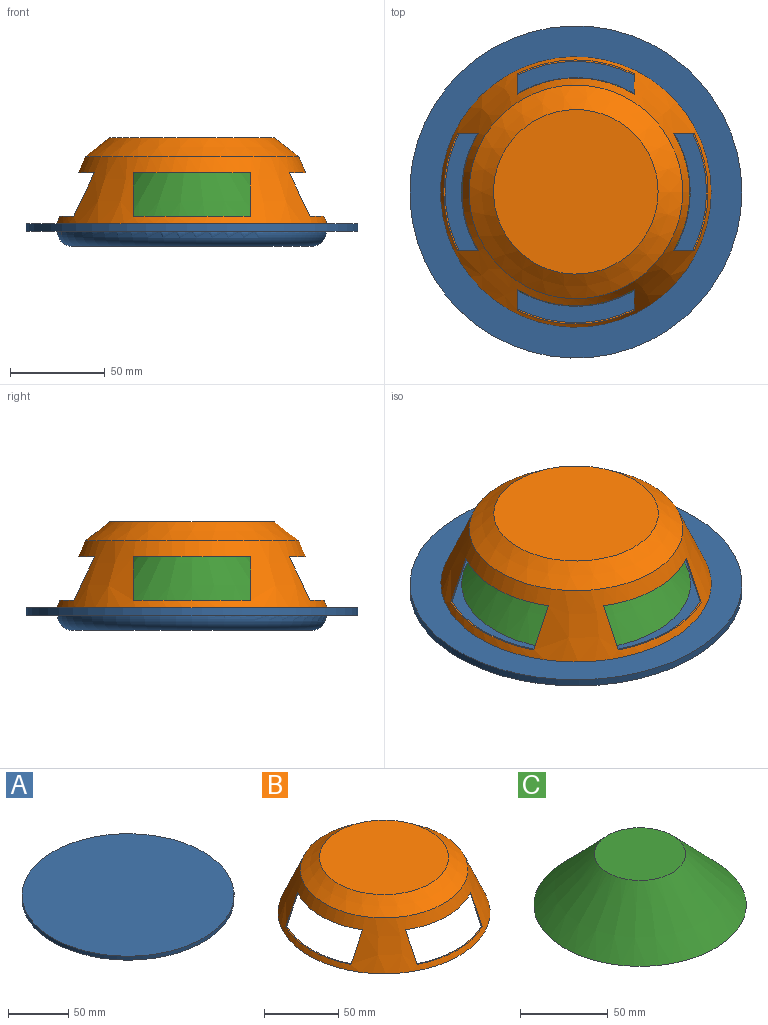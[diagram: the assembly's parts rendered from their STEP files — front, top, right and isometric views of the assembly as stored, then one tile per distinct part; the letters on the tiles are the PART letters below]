
ASSEMBLY  parts=3 mates=2
PART A: 5 faces, bbox 175.6x175.6x13.4 mm
  f0: plane 175.6x175.6mm, normal (0,0,-1), area 8353.8mm2, adj f1,f3
  f1: cylinder r=87.8mm len=175.6mm, axis (0,0,1), area 2206.7mm2, adj f0,f2
  f2: plane 175.6x175.6mm, normal (0,0,1), area 24218mm2, adj f1
  f3: torus R=63.24mm, axis (0,0,-1), area 9762.8mm2, adj f0,f4
  f4: plane 110.84x110.84mm, normal (0,0,-1), area 9649mm2, adj f3
PART B: 23 faces, bbox 143x143x45.6 mm
  f0: plane 62x8.11mm, normal (0,0,1), area 48.8mm2, adj f1,f3,f12,f13
  f1: plane 23x11.94mm, normal (0,1,0), area 19.9mm2, adj f0,f2,f12,f13
  f2: plane 62x9.5mm, normal (0,0,-1), area 49.5mm2, adj f1,f3,f12,f13
  f3: plane 23x11.94mm, normal (0,-1,0), area 19.9mm2, adj f0,f2,f12,f13
  f4: plane 62x8.11mm, normal (0,0,1), area 48.8mm2, adj f5,f7,f12,f13
  f5: plane 23x11.94mm, normal (1,0,0), area 19.9mm2, adj f4,f6,f12,f13
  f6: plane 62x9.5mm, normal (0,0,-1), area 49.5mm2, adj f5,f7,f12,f13
  f7: plane 23x11.94mm, normal (-1,0,0), area 19.9mm2, adj f4,f6,f12,f13
  f8: plane 62x8.11mm, normal (0,0,1), area 48.8mm2, adj f9,f11,f12,f13
  f9: plane 23x11.94mm, normal (0,-1,0), area 19.9mm2, adj f8,f10,f12,f13
  f10: plane 62x9.5mm, normal (0,0,-1), area 49.5mm2, adj f9,f11,f12,f13
  f11: plane 23x11.94mm, normal (0,1,0), area 19.9mm2, adj f8,f10,f12,f13
  f12: cone r=71.5mm half-angle=22.9deg, axis (0,0,-1), area 9064.1mm2, adj f0,f1,f2,f3,f4,f5,f6,f7
  f13: cone r=70.86mm half-angle=22.9deg, axis (0,0,-1), area 8704.3mm2, adj f0,f1,f2,f3,f4,f5,f6,f7
  f14: plane 87x87mm, normal (0,0,1), area 5944.7mm2, adj f15
  f15: cone r=56.5mm half-angle=52.4deg, axis (0,0,-1), area 5152.6mm2, adj f12,f14
  f16: plane 143x143mm, normal (0,0,-1), area 339.5mm2, adj f12,f13
  f17: plane 86.52x86.52mm, normal (0,0,-1), area 5879.8mm2, adj f18
  f18: cone r=56.07mm half-angle=52.4deg, axis (0,0,-1), area 4979.1mm2, adj f13,f17
  f19: plane 62x8.11mm, normal (0,0,1), area 48.8mm2, adj f12,f13,f20,f22
  f20: plane 23x11.94mm, normal (-1,0,0), area 19.9mm2, adj f12,f13,f19,f21
  f21: plane 62x9.5mm, normal (0,0,-1), area 49.5mm2, adj f12,f13,f20,f22
  f22: plane 23x11.94mm, normal (1,0,0), area 19.9mm2, adj f12,f13,f19,f21
PART C: 3 faces, bbox 121x121x35.6 mm
  f0: plane 52x52mm, normal (0,0,1), area 2123.7mm2, adj f1
  f1: cone r=60.5mm half-angle=44.1deg, axis (0,0,-1), area 13463.9mm2, adj f0,f2
  f2: plane 121x121mm, normal (0,0,-1), area 11499mm2, adj f1
PLACE A t=(163.14,-92.89,80.12)mm
PLACE B t=(163.14,-92.89,80.12)mm
PLACE C t=(163.14,-92.89,80.12)mm
MATE cylindrical B.f12 <-> A.f1  axis (0,0,-1) through (163.14,-92.89,80.12)mm
MATE cylindrical A.f1 <-> C.f1  axis (0,0,1) through (163.14,-92.89,80.12)mm
